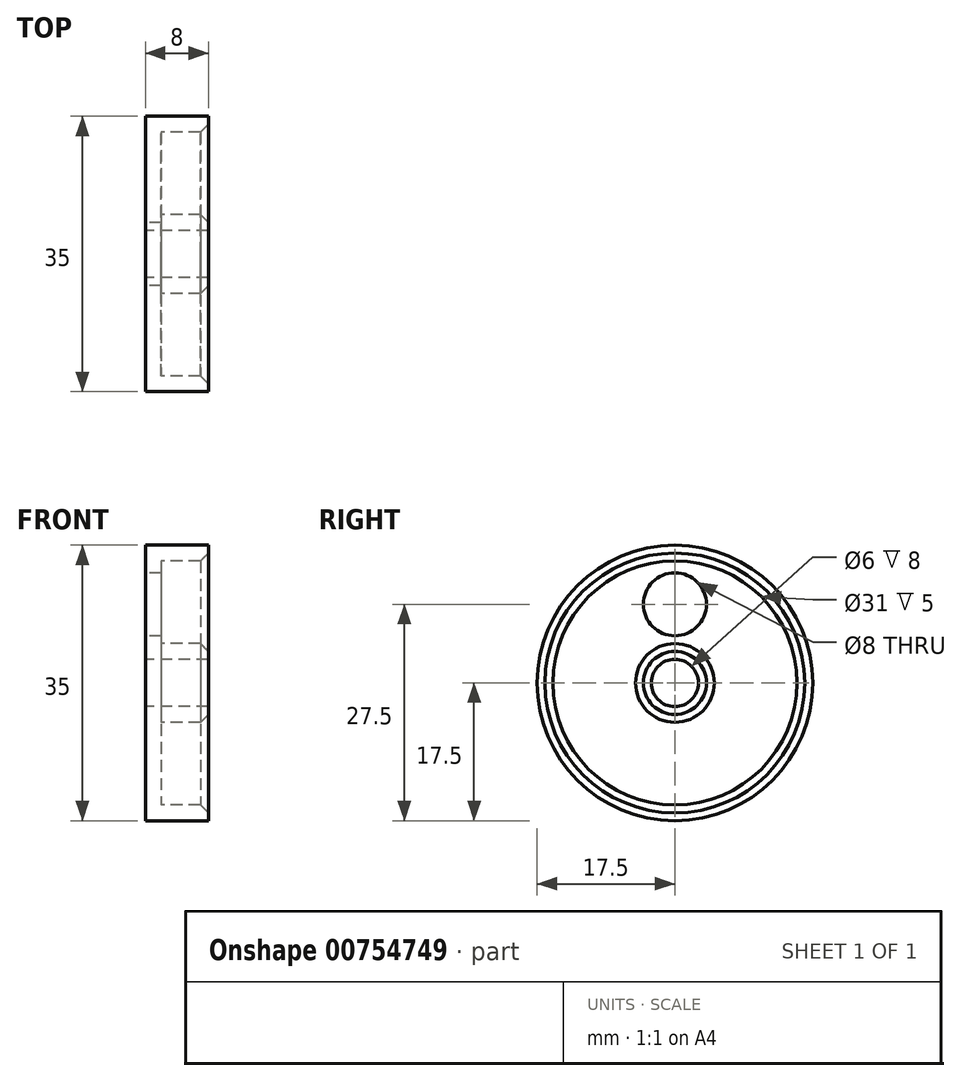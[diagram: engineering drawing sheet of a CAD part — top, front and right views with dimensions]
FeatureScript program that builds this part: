
annotation { "Feature Type Name" : "Feature", "Feature Type Description" : "" }
export const myFeature = defineFeature(function(context is Context, id is Id, definition is map)
    precondition{}
    {
        {
            var Q0;
            Q0=qCreatedBy(makeId("Top.planeOp"),FACE);
            var sketch = newSketch(context, id + "F0", { "sketchPlane" : qUnion([Q0])});
            skLineSegment(sketch, "E0.bottom", {"start": v(0, 0) * mm, "end": v(8, 0) * mm});
            skLineSegment(sketch, "E0.top", {"start": v(0, 17.5) * mm, "end": v(8, 17.5) * mm});
            skLineSegment(sketch, "E0.left", {"start": v(0, 0) * mm, "end": v(0, 17.5) * mm});
            skLineSegment(sketch, "E0.right", {"start": v(8, 0) * mm, "end": v(8, 17.5) * mm});
            skSolve(sketch);
        }
        {
            var Q0;
            Q0=makeQuery(id+"F0.imprint","IMPRINT",FACE,{"disambiguationData":[TD([[makeQuery(id+"F0.imprint","IMPRINT",EDGE,{"derivedFrom":sQuery(id+"F0.wireOp",EDGE,"E0.bottom")}),1.0]])]});
            var Q1;
            Q1=sQuery(id+"F0.wireOp",EDGE,"E0.bottom");
            revolve(context, id + "F1", {"surfaceOperationType" : NewSurfaceOperationType.NEW, "entities" : qUnion([Q0]), "axis" : qUnion([Q1]), "revolveType" : RevolveType.FULL});
        }
        {
            var Q0;
            Q0=qCreatedBy(makeId("Right.planeOp"),FACE);
            var sketch = newSketch(context, id + "F2", { "sketchPlane" : qUnion([Q0])});
            skPoint(sketch, "E1", {"position": v(0, 0) * mm});
            skSolve(sketch);
        }
        {
            var Q0;
            Q0=sQuery(id+"F2.wireOp",VERTEX,"E1");
            var Q1;
            Q1=makeQuery(id+"F1.opRevolve","SWEPT_BODY",BODY,{"disambiguationData":[OSD([sQuery(id+"F0.wireOp",EDGE,"E0.bottom"),sQuery(id+"F0.wireOp",EDGE,"E0.top"),sQuery(id+"F0.wireOp",EDGE,"E0.left"),sQuery(id+"F0.wireOp",EDGE,"E0.right")])]});
            hole(context, id + "F3", {"style" : HoleStyle.SIMPLE, "endStyle" : HoleEndStyle.THROUGH, "oppositeDirection" : true, "holeDiameter" : 6 * mm, "majorDiameter" : 5 * mm, "isTappedThrough" : true, "tappedDepth" : 12 * mm, "tapClearance" : 3, "locations" : qUnion([Q0]), "scope" : qUnion([Q1])});
        }
        {
            var Q0;
            Q0=makeQuery(id+"F1.opRevolve","SWEPT_FACE",FACE,{"disambiguationData":[OSD([sQuery(id+"F0.wireOp",EDGE,"E0.right")])]});
            var Q1;
            Q1=makeQuery(id+"F1.opRevolve","SWEPT_BODY",BODY,{"disambiguationData":[OSD([sQuery(id+"F0.wireOp",EDGE,"E0.bottom"),sQuery(id+"F0.wireOp",EDGE,"E0.top"),sQuery(id+"F0.wireOp",EDGE,"E0.left"),sQuery(id+"F0.wireOp",EDGE,"E0.right")])]});
            shell(context, id + "F4", {"entities" : qUnion([Q0]), "parts" : qUnion([Q1]), "thickness" : 2 * mm});
        }
        {
            var Q0;
            Q0=makeQuery(id+"F1.opRevolve","SWEPT_FACE",FACE,{"disambiguationData":[OSD([sQuery(id+"F0.wireOp",EDGE,"E0.left")])]});
            var sketch = newSketch(context, id + "F5", { "sketchPlane" : qUnion([Q0])});
            skPoint(sketch, "E2", {"position": v(0, 10) * mm});
            skSolve(sketch);
        }
        {
            var Q0;
            Q0=sQuery(id+"F5.wireOp",VERTEX,"E2");
            var Q1;
            Q1=makeQuery(id+"F1.opRevolve","SWEPT_BODY",BODY,{"disambiguationData":[OSD([sQuery(id+"F0.wireOp",EDGE,"E0.bottom"),sQuery(id+"F0.wireOp",EDGE,"E0.top"),sQuery(id+"F0.wireOp",EDGE,"E0.left"),sQuery(id+"F0.wireOp",EDGE,"E0.right")])]});
            hole(context, id + "F6", {"style" : HoleStyle.SIMPLE, "endStyle" : HoleEndStyle.THROUGH, "holeDiameter" : 8 * mm, "majorDiameter" : 5 * mm, "isTappedThrough" : true, "tappedDepth" : 12 * mm, "tapClearance" : 3, "locations" : qUnion([Q0]), "scope" : qUnion([Q1])});
        }
        {
            var Q0;
            Q0=makeQuery(id+"F4.opShell","OFFSET_EDGE",EDGE,{"disambiguationData":[OSD([sQuery(id+"F0.wireOp",EDGE,"E0.right"),sQuery(id+"F3.hole-0.sketch.wireOp",EDGE,"core_line_2")])]});
            chamfer(context, id + "F7", {"entities" : qUnion([Q0]), "width" : 1 * mm, "tangentPropagation" : true});
        }
    });
